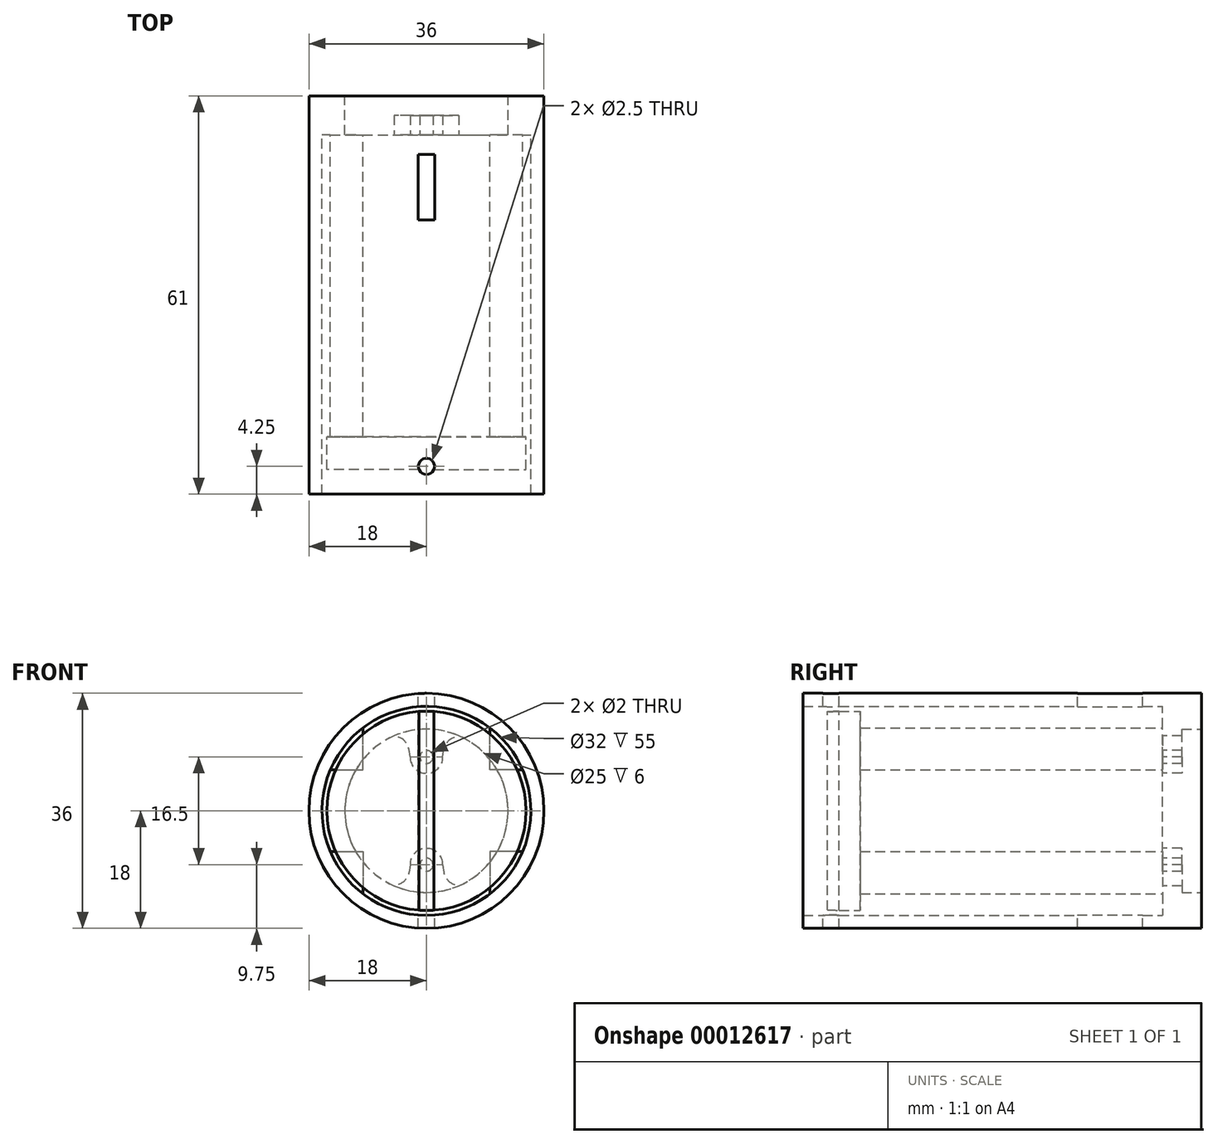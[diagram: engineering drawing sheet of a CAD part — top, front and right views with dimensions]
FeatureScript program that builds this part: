
annotation { "Feature Type Name" : "Feature", "Feature Type Description" : "" }
export const myFeature = defineFeature(function(context is Context, id is Id, definition is map)
    precondition{}
    {
        {
            var Q0;
            Q0=qCreatedBy(makeId("Front.planeOp"),FACE);
            var sketch = newSketch(context, id + "F0", { "sketchPlane" : qUnion([Q0])});
            skCircle(sketch, "E0", {"center": v(0, 0) * mm, "radius": 12.5 * mm});
            skCircle(sketch, "E1", {"center": v(0, 0) * mm, "radius": 18 * mm});
            skSolve(sketch);
        }
        {
            var Q0;
            Q0=makeQuery(id+"F0.imprint","IMPRINT",FACE,{"disambiguationData":[TD([[makeQuery(id+"F0.imprint","IMPRINT",EDGE,{"derivedFrom":sQuery(id+"F0.wireOp",EDGE,"E0")}),-1.0]])]});
            extrude(context, id + "F1", {"entities" : qUnion([Q0]), "depth" : 6 * mm});
        }
        {
            var Q0;
            Q0=makeQuery(id+"F1.opExtrude","CAP_FACE",FACE,{"disambiguationData":[OSD([sQuery(id+"F0.wireOp",EDGE,"E0"),sQuery(id+"F0.wireOp",EDGE,"1bf179f9-79cc-4984-950a-c811c04e8cd8.0")])],"isStart":false});
            var sketch = newSketch(context, id + "F2", { "sketchPlane" : qUnion([Q0])});
            skCircle(sketch, "E2", {"center": v(0, 0) * mm, "radius": 8.25 * mm, "construction": true});
            skCircle(sketch, "E3", {"center": v(0, 8.25) * mm, "radius": 1 * mm});
            skArc(sketch, "E4", {"start": v(-2.5, 8.25) * mm, "mid": v(0, 5.75) * mm, "end": v(2.5, 8.25) * mm});
            skLineSegment(sketch, "E5", {"start": v(0, 8.25) * mm, "end": v(-4.98, 8.25) * mm, "construction": true});
            skFitSpline(sketch, "E6", {"points": [v(-2.5, 8.25) * mm, v(-2.9, 10.13) * mm, v(-3.42, 10.78) * mm, v(-4.14, 11.24) * mm, v(-4.96, 11.47) * mm], "startDerivative": vector(-1.44, 11.98) * mm, "endDerivative": vector(-3.8, 1.18) * mm});
            skArc(sketch, "E7.0", {"start": v(4.96, 11.47) * mm, "mid": v(0, 12.5) * mm, "end": v(-4.96, 11.47) * mm});
            skFitSpline(sketch, "E8.0.MirrorCS", {"points": [v(2.5, 8.25) * mm, v(2.9, 10.13) * mm, v(3.42, 10.78) * mm, v(4.14, 11.24) * mm, v(4.96, 11.47) * mm], "startDerivative": vector(1.44, 11.98) * mm, "endDerivative": vector(3.8, 1.18) * mm});
            skFitSpline(sketch, "E9.0.MirrorCS", {"points": [v(-2.5, -8.25) * mm, v(-2.9, -10.13) * mm, v(-3.42, -10.78) * mm, v(-4.14, -11.24) * mm, v(-4.96, -11.47) * mm], "startDerivative": vector(-1.44, -11.98) * mm, "endDerivative": vector(-3.8, -1.18) * mm});
            skFitSpline(sketch, "E9.1.MirrorCS", {"points": [v(2.5, -8.25) * mm, v(2.9, -10.13) * mm, v(3.42, -10.78) * mm, v(4.14, -11.24) * mm, v(4.96, -11.47) * mm], "startDerivative": vector(1.44, -11.98) * mm, "endDerivative": vector(3.8, -1.18) * mm});
            skCircle(sketch, "E9.2.MirrorC", {"center": v(0, -8.25) * mm, "radius": 1 * mm});
            skArc(sketch, "E9.3.MirrorCS", {"start": v(-2.5, -8.25) * mm, "mid": v(0, -5.75) * mm, "end": v(2.5, -8.25) * mm});
            skLineSegment(sketch, "E9.4.MirrorCS", {"start": v(0, -8.25) * mm, "end": v(-4.98, -8.25) * mm, "construction": true});
            skArc(sketch, "E9.5.MirrorCS", {"start": v(4.96, -11.47) * mm, "mid": v(0, -12.5) * mm, "end": v(-4.96, -11.47) * mm});
            skSolve(sketch);
        }
        {
            var Q0;
            Q0=makeQuery(id+"F2.imprint","IMPRINT",FACE,{"disambiguationData":[TD([[makeQuery(id+"F2.imprint","IMPRINT",EDGE,{"derivedFrom":sQuery(id+"F2.wireOp",EDGE,"E9.0.MirrorCS")}),1.0]])]});
            var Q1;
            Q1=makeQuery(id+"F2.imprint","IMPRINT",FACE,{"disambiguationData":[TD([[makeQuery(id+"F2.imprint","IMPRINT",EDGE,{"derivedFrom":sQuery(id+"F2.wireOp",EDGE,"E3")}),-1.0]])]});
            extrude(context, id + "F3", {"entities" : qUnion([Q0, Q1]), "operationType" : NewBodyOperationType.ADD, "oppositeDirection" : true, "depth" : 3 * mm});
        }
        {
            var Q0;
            Q0=makeQuery(id+"F3.boolean.opBoolean","MERGE",FACE,{"derivedFrom":[makeQuery(id+"F1.opExtrude","CAP_FACE",FACE,{"disambiguationData":[OSD([sQuery(id+"F0.wireOp",EDGE,"E0"),sQuery(id+"F0.wireOp",EDGE,"E1")])],"isStart":false}),makeQuery(id+"F3.opExtrude","CAP_FACE",FACE,{"disambiguationData":[OSD([sQuery(id+"F2.wireOp",EDGE,"E3"),sQuery(id+"F2.wireOp",EDGE,"E4"),sQuery(id+"F2.wireOp",EDGE,"E6"),sQuery(id+"F2.wireOp",EDGE,"E7.0"),sQuery(id+"F2.wireOp",EDGE,"E8.0.MirrorCS")])],"isStart":true}),makeQuery(id+"F3.opExtrude","CAP_FACE",FACE,{"disambiguationData":[OSD([sQuery(id+"F2.wireOp",EDGE,"E9.0.MirrorCS"),sQuery(id+"F2.wireOp",EDGE,"E9.1.MirrorCS"),sQuery(id+"F2.wireOp",EDGE,"E9.2.MirrorC"),sQuery(id+"F2.wireOp",EDGE,"E9.3.MirrorCS"),sQuery(id+"F2.wireOp",EDGE,"E9.5.MirrorCS")])],"isStart":true})]});
            var sketch = newSketch(context, id + "F4", { "sketchPlane" : qUnion([Q0])});
            skCircle(sketch, "E10.0", {"center": v(0, 0) * mm, "radius": 18 * mm});
            skCircle(sketch, "E11.0", {"center": v(0, 0) * mm, "radius": 16 * mm});
            skSolve(sketch);
        }
        {
            var Q0;
            Q0 = qSketchRegion(id + "F4", true);
            extrude(context, id + "F5", {"entities" : qUnion([Q0]), "operationType" : NewBodyOperationType.ADD, "depth" : 55 * mm});
        }
        {
            var Q0;
            Q0=makeQuery(id+"F3.boolean.opBoolean","MERGE",FACE,{"derivedFrom":[makeQuery(id+"F1.opExtrude","CAP_FACE",FACE,{"disambiguationData":[OSD([sQuery(id+"F0.wireOp",EDGE,"E0"),sQuery(id+"F0.wireOp",EDGE,"E1")])],"isStart":false}),makeQuery(id+"F3.opExtrude","CAP_FACE",FACE,{"disambiguationData":[OSD([sQuery(id+"F2.wireOp",EDGE,"E3"),sQuery(id+"F2.wireOp",EDGE,"E4"),sQuery(id+"F2.wireOp",EDGE,"E6"),sQuery(id+"F2.wireOp",EDGE,"E7.0"),sQuery(id+"F2.wireOp",EDGE,"E8.0.MirrorCS")])],"isStart":true}),makeQuery(id+"F3.opExtrude","CAP_FACE",FACE,{"disambiguationData":[OSD([sQuery(id+"F2.wireOp",EDGE,"E9.0.MirrorCS"),sQuery(id+"F2.wireOp",EDGE,"E9.1.MirrorCS"),sQuery(id+"F2.wireOp",EDGE,"E9.2.MirrorC"),sQuery(id+"F2.wireOp",EDGE,"E9.3.MirrorCS"),sQuery(id+"F2.wireOp",EDGE,"E9.5.MirrorCS")])],"isStart":true})]});
            var sketch = newSketch(context, id + "F6", { "sketchPlane" : qUnion([Q0])});
            skLineSegment(sketch, "E12.rect.bottom", {"start": v(14.73, 6.25) * mm, "end": v(-14.73, 6.25) * mm, "construction": true});
            skLineSegment(sketch, "E12.rect.top", {"start": v(14.73, -6.25) * mm, "end": v(-14.73, -6.25) * mm, "construction": true});
            skLineSegment(sketch, "E12.rect.left", {"start": v(14.73, 6.25) * mm, "end": v(14.73, -6.25) * mm, "construction": true});
            skLineSegment(sketch, "E12.rect.right", {"start": v(-14.73, 6.25) * mm, "end": v(-14.73, -6.25) * mm, "construction": true});
            skPoint(sketch, "E12.rect.middle", {"position": v(0, 0) * mm});
            skArc(sketch, "E13.0", {"start": v(14.73, 6.25) * mm, "mid": v(12.65, 9.8) * mm, "end": v(9.73, 12.7) * mm});
            skLineSegment(sketch, "E14", {"start": v(14.73, 6.25) * mm, "end": v(9.73, 6.25) * mm});
            skLineSegment(sketch, "E15", {"start": v(9.73, 6.25) * mm, "end": v(9.73, 12.7) * mm});
            skLineSegment(sketch, "E16.0.MirrorCS", {"start": v(14.73, -6.25) * mm, "end": v(9.73, -6.25) * mm});
            skArc(sketch, "E17.0.MirrorCS", {"start": v(14.73, -6.25) * mm, "mid": v(12.65, -9.8) * mm, "end": v(9.73, -12.7) * mm});
            skLineSegment(sketch, "E18.0.MirrorCS", {"start": v(9.73, -6.25) * mm, "end": v(9.73, -12.7) * mm});
            skLineSegment(sketch, "E19.0.MirrorCS", {"start": v(-9.73, 6.25) * mm, "end": v(-9.73, 12.7) * mm});
            skLineSegment(sketch, "E20.0.MirrorCS", {"start": v(-14.73, 6.25) * mm, "end": v(-9.73, 6.25) * mm});
            skArc(sketch, "E21.0.MirrorCS", {"start": v(-14.73, 6.25) * mm, "mid": v(-12.65, 9.8) * mm, "end": v(-9.73, 12.7) * mm});
            skLineSegment(sketch, "E22.0.MirrorCS", {"start": v(-9.73, -6.25) * mm, "end": v(-9.73, -12.7) * mm});
            skLineSegment(sketch, "E23.0.MirrorCS", {"start": v(-14.73, -6.25) * mm, "end": v(-9.73, -6.25) * mm});
            skArc(sketch, "E24.0.MirrorCS", {"start": v(-14.73, -6.25) * mm, "mid": v(-12.65, -9.8) * mm, "end": v(-9.73, -12.7) * mm});
            skSolve(sketch);
        }
        {
            var Q0;
            Q0 = qSketchRegion(id + "F6", true);
            extrude(context, id + "F7", {"entities" : qUnion([Q0]), "operationType" : NewBodyOperationType.ADD, "depth" : 46.25 * mm});
        }
        {
            var Q0;
            Q0=makeQuery(id+"F7.opExtrude","CAP_FACE",FACE,{"disambiguationData":[OSD([sQuery(id+"F6.wireOp",EDGE,"E13.0"),sQuery(id+"F6.wireOp",EDGE,"E14"),sQuery(id+"F6.wireOp",EDGE,"E15")])],"isStart":false});
            var sketch = newSketch(context, id + "F8", { "sketchPlane" : qUnion([Q0])});
            skCircle(sketch, "E25.0", {"center": v(0, 0) * mm, "radius": 15.25 * mm});
            skSolve(sketch);
        }
        {
            var Q0;
            Q0 = qSketchRegion(id + "F8", true);
            extrude(context, id + "F9", {"entities" : qUnion([Q0]), "depth" : 5 * mm});
        }
        {
            var Q0;
            Q0=qCreatedBy(makeId("Top.planeOp"),FACE);
            var sketch = newSketch(context, id + "F10", { "sketchPlane" : qUnion([Q0])});
            skLineSegment(sketch, "E26.rect.bottom", {"start": v(1.25, -9) * mm, "end": v(-1.25, -9) * mm});
            skLineSegment(sketch, "E26.rect.top", {"start": v(1.25, -19) * mm, "end": v(-1.25, -19) * mm});
            skLineSegment(sketch, "E26.rect.left", {"start": v(1.25, -9) * mm, "end": v(1.25, -19) * mm});
            skLineSegment(sketch, "E26.rect.right", {"start": v(-1.25, -9) * mm, "end": v(-1.25, -19) * mm});
            skPoint(sketch, "E26.rect.middle", {"position": v(0, -14) * mm});
            skSolve(sketch);
        }
        {
            var Q0;
            Q0 = qSketchRegion(id + "F10", true);
            extrude(context, id + "F11", {"entities" : qUnion([Q0]), "operationType" : NewBodyOperationType.REMOVE, "endBound" : BoundingType.THROUGH_ALL, "oppositeDirection" : true, "depth" : 25 * mm, "hasSecondDirection" : true, "secondDirectionBound" : SecondDirectionBoundingType.THROUGH_ALL, "secondDirectionOppositeDirection" : false, "secondDirectionDepth" : 25 * mm});
        }
        {
            var Q0;
            Q0=qCreatedBy(makeId("Top.planeOp"),FACE);
            var sketch = newSketch(context, id + "F12", { "sketchPlane" : qUnion([Q0])});
            skArc(sketch, "E27", {"start": v(18, -51.5) * mm, "mid": v(16.77, -53) * mm, "end": v(18, -54.5) * mm});
            skLineSegment(sketch, "E28.0", {"start": v(18, -61) * mm, "end": v(-18, -61) * mm, "construction": true});
            skLineSegment(sketch, "E29", {"start": v(18, -61) * mm, "end": v(18, 3.04) * mm, "construction": true});
            skArc(sketch, "E30.0.1.0", {"start": v(18, -46.5) * mm, "mid": v(16.77, -48) * mm, "end": v(18, -49.5) * mm});
            skLineSegment(sketch, "E30.direction1", {"start": v(18, -54.5) * mm, "end": v(43, -54.5) * mm, "construction": true});
            skLineSegment(sketch, "E30.direction2", {"start": v(18, -54.5) * mm, "end": v(18, -49.5) * mm, "construction": true});
            skLineSegment(sketch, "E31", {"start": v(0, -61) * mm, "end": v(0, 14.38) * mm, "construction": true});
            skSolve(sketch);
        }
        {
            var Q0;
            Q0=qCreatedBy(makeId("Top.planeOp"),FACE);
            cPlane(context, id + "F13", {"entities" : qUnion([Q0]), "cplaneType" : CPlaneType.OFFSET, "offset" : 25 * mm, "width" : 150 * mm, "height" : 150 * mm});
        }
        {
            var Q0;
            Q0=qCreatedBy(id+"F13.planeOp",FACE);
            var sketch = newSketch(context, id + "F14", { "sketchPlane" : qUnion([Q0])});
            skCircle(sketch, "E32", {"center": v(0, -56.75) * mm, "radius": 1.25 * mm});
            skSolve(sketch);
        }
        {
            var Q0;
            Q0 = qSketchRegion(id + "F14", true);
            extrude(context, id + "F15", {"entities" : qUnion([Q0]), "operationType" : NewBodyOperationType.REMOVE, "endBound" : BoundingType.THROUGH_ALL, "oppositeDirection" : true, "depth" : 15 * mm});
        }
    });
